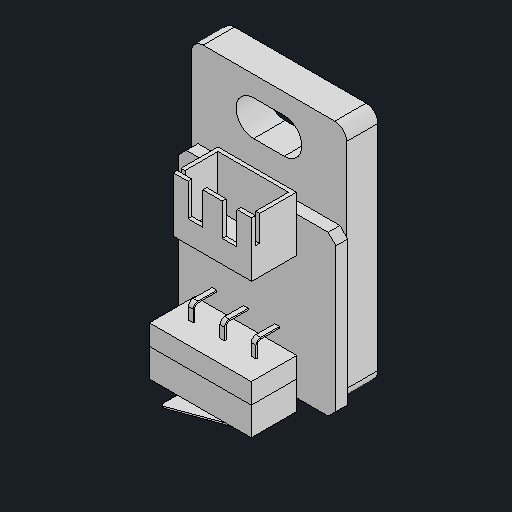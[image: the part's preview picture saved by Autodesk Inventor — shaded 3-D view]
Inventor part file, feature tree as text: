
AUTODESK INVENTOR PART (.ipt)
format: ipt  version: 2024.2 (Build 282272000, 272)  size: 182,784 bytes
history: native  units: mm
features: other x23, extrude x2, chamfer x1
ambient origin geometry x8: Origin, YZ Plane, XZ Plane, XY Plane, X Axis, Y Axis, Z Axis, Center Point
bodies: Body1 (feature_tree), Body2 (feature_tree), Body3 (feature_tree), Body4 (feature_tree), Body5 (feature_tree), Body6 (feature_tree), Body7 (feature_tree), Body8 (feature_tree), Body9 (feature_tree), Body10 (feature_tree), Body11 (feature_tree), Body12 (feature_tree), Body13 (feature_tree)
feature tree (26):
  other  "솔리드1"
  other  "솔리드2"
  other  "솔리드3"
  other  "솔리드4"
  other  "솔리드5"
  other  "솔리드6"
  other  "솔리드7"
  other  "솔리드8"
  other  "솔리드9"
  other  "솔리드10"
  other  "솔리드11"
  other  "솔리드12"
  other  "솔리드13"
  other  "Cut-Extrude1"
  chamfer  "Chamfer1"  [1 undecoded]
  other  "Split1[1]"
  other  "Split1[2]"
  other  "Cut-Extrude3"
  other  "Boss-Extrude5"
  extrude  "Extrude-Thin2"  [1 undecoded]
  other  "LPattern1[1]"
  other  "LPattern1[2]"
  extrude  "Extrude-Thin3"  [1 undecoded]
  other  "LPattern2[1]"
  other  "LPattern2[2]"
  other  "Cut-Extrude4"
note: 3 required parameter values undecoded (feature->parameter linkage not recoverable at this tier; creation-order binding heuristic only, values carry confidence <= 0.55)
